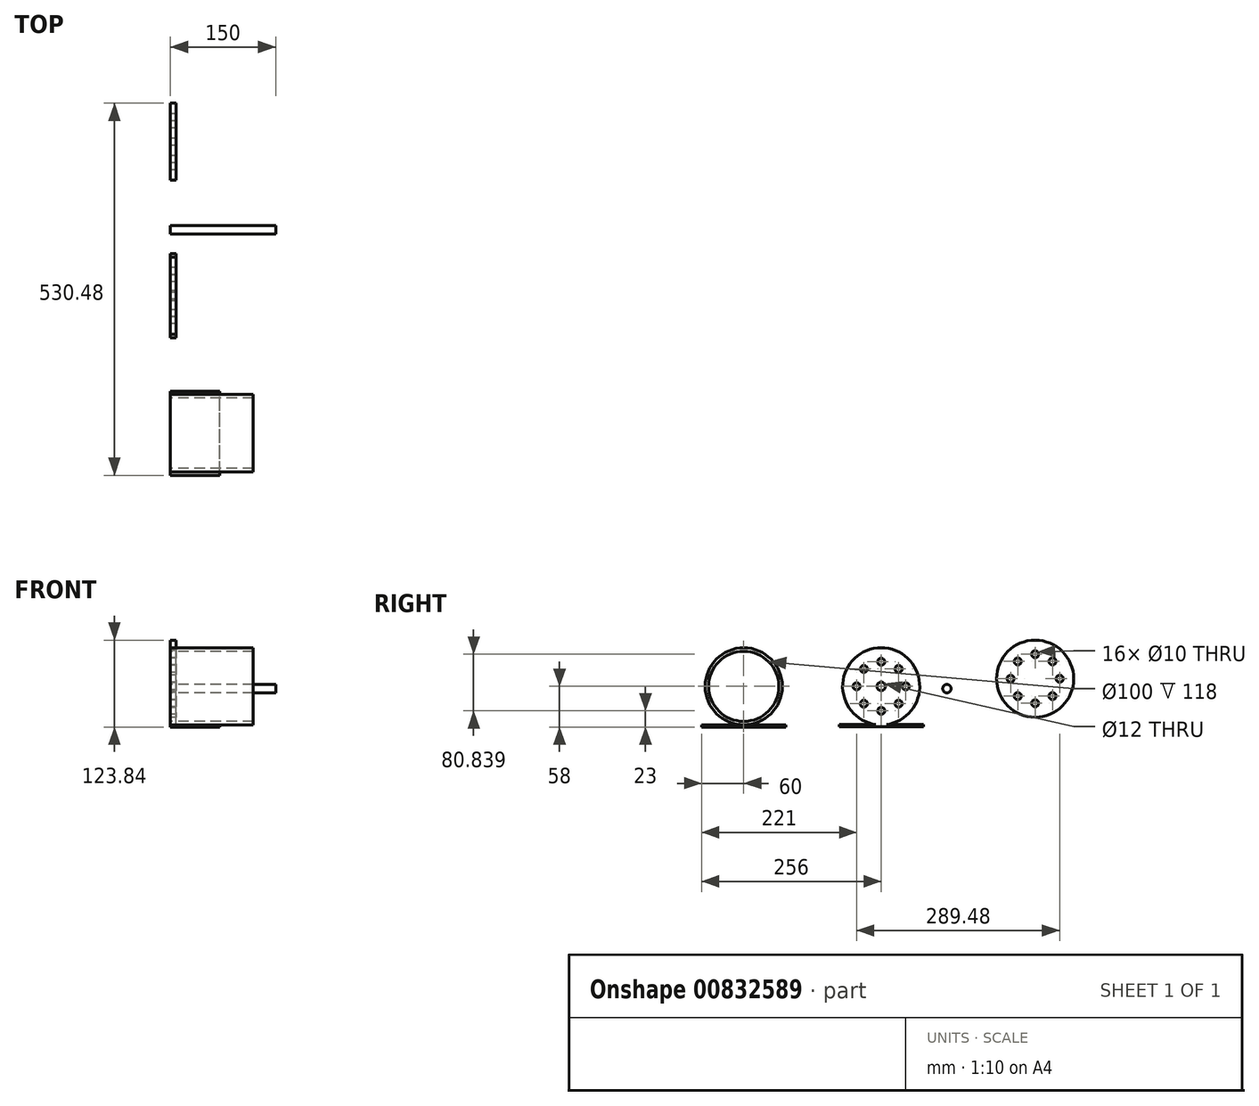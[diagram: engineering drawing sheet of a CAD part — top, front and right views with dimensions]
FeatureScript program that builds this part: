
annotation { "Feature Type Name" : "Feature", "Feature Type Description" : "" }
export const myFeature = defineFeature(function(context is Context, id is Id, definition is map)
    precondition{}
    {
        {
            var Q0;
            Q0=qCreatedBy(makeId("Right.planeOp"),FACE);
            var sketch = newSketch(context, id + "F0", { "sketchPlane" : qUnion([Q0])});
            skArc(sketch, "E0", {"start": v(7.4, -54.5) * mm, "mid": v(0, 55) * mm, "end": v(-7.4, -54.5) * mm});
            skCircle(sketch, "E1", {"center": v(0, 0) * mm, "radius": 6 * mm});
            skCircle(sketch, "E2", {"center": v(0, 35) * mm, "radius": 5 * mm});
            skCircle(sketch, "E3.1.0", {"center": v(-24.75, 24.75) * mm, "radius": 5 * mm});
            skCircle(sketch, "E3.2.0", {"center": v(-35, 0) * mm, "radius": 5 * mm});
            skCircle(sketch, "E3.3.0", {"center": v(-24.75, -24.75) * mm, "radius": 5 * mm});
            skCircle(sketch, "E3.4.0", {"center": v(0, -35) * mm, "radius": 5 * mm});
            skCircle(sketch, "E3.5.0", {"center": v(24.75, -24.75) * mm, "radius": 5 * mm});
            skCircle(sketch, "E3.6.0", {"center": v(35, 0) * mm, "radius": 5 * mm});
            skCircle(sketch, "E3.7.0", {"center": v(24.75, 24.75) * mm, "radius": 5 * mm});
            skLineSegment(sketch, "E4", {"start": v(0, 0) * mm, "end": v(0, -55) * mm});
            skLineSegment(sketch, "E5", {"start": v(60, -55) * mm, "end": v(60, -57.5) * mm});
            skLineSegment(sketch, "E6", {"start": v(60, -57.5) * mm, "end": v(-60, -57.5) * mm});
            skLineSegment(sketch, "E7", {"start": v(-60, -57.5) * mm, "end": v(-60, -54.5) * mm});
            skLineSegment(sketch, "E8", {"start": v(-60, -54.5) * mm, "end": v(-7.4, -54.5) * mm});
            skLineSegment(sketch, "E9", {"start": v(7.4, -54.5) * mm, "end": v(60, -54.5) * mm});
            skLineSegment(sketch, "E10", {"start": v(60, -54.5) * mm, "end": v(60, -55) * mm});
            skPoint(sketch, "E11.orphan", {"position": v(0, -54.5) * mm});
            skSolve(sketch);
        }
        {
            var Q0;
            Q0=makeQuery(id+"F0.imprint","IMPRINT",FACE,{"disambiguationData":[TD([[makeQuery(id+"F0.imprint","IMPRINT",EDGE,{"derivedFrom":sQuery(id+"F0.wireOp",EDGE,"E0")}),1.0]])]});
            extrude(context, id + "F1", {"entities" : qUnion([Q0]), "depth" : 8 * mm, "offsetDistance" : 25 * mm});
        }
        {
            var Q0;
            Q0=qCreatedBy(makeId("Right.planeOp"),FACE);
            var sketch = newSketch(context, id + "F2", { "sketchPlane" : qUnion([Q0])});
            skCircle(sketch, "E12", {"center": v(93.73, -3.28) * mm, "radius": 6 * mm});
            skSolve(sketch);
        }
        {
            var Q0;
            Q0=makeQuery(id+"F2.imprint","IMPRINT",FACE,{"disambiguationData":[TD([[makeQuery(id+"F2.imprint","IMPRINT",EDGE,{"derivedFrom":sQuery(id+"F2.wireOp",EDGE,"E12")}),1.0]])]});
            extrude(context, id + "F3", {"entities" : qUnion([Q0]), "depth" : 150 * mm, "offsetDistance" : 25 * mm});
        }
        {
            var Q0;
            Q0=qCreatedBy(makeId("Right.planeOp"),FACE);
            var sketch = newSketch(context, id + "F4", { "sketchPlane" : qUnion([Q0])});
            skCircle(sketch, "E13", {"center": v(219.48, 10.84) * mm, "radius": 55 * mm});
            skCircle(sketch, "E14", {"center": v(219.48, 45.84) * mm, "radius": 5 * mm});
            skCircle(sketch, "E15.1.0", {"center": v(194.73, 35.59) * mm, "radius": 5 * mm});
            skCircle(sketch, "E15.2.0", {"center": v(184.48, 10.84) * mm, "radius": 5 * mm});
            skCircle(sketch, "E15.3.0", {"center": v(194.73, -13.9) * mm, "radius": 5 * mm});
            skCircle(sketch, "E15.4.0", {"center": v(219.48, -24.16) * mm, "radius": 5 * mm});
            skCircle(sketch, "E15.5.0", {"center": v(244.23, -13.9) * mm, "radius": 5 * mm});
            skCircle(sketch, "E15.6.0", {"center": v(254.48, 10.84) * mm, "radius": 5 * mm});
            skCircle(sketch, "E15.7.0", {"center": v(244.23, 35.59) * mm, "radius": 5 * mm});
            skSolve(sketch);
        }
        {
            var Q0;
            Q0=makeQuery(id+"F4.imprint","IMPRINT",FACE,{"disambiguationData":[TD([[makeQuery(id+"F4.imprint","IMPRINT",EDGE,{"derivedFrom":sQuery(id+"F4.wireOp",EDGE,"E13")}),1.0]])]});
            extrude(context, id + "F5", {"entities" : qUnion([Q0]), "depth" : 8 * mm, "offsetDistance" : 25 * mm});
        }
        {
            var Q0;
            Q0=qCreatedBy(makeId("Right.planeOp"),FACE);
            var sketch = newSketch(context, id + "F6", { "sketchPlane" : qUnion([Q0])});
            skCircle(sketch, "E16", {"center": v(-196, 0) * mm, "radius": 55 * mm});
            skCircle(sketch, "E17", {"center": v(-196, 0) * mm, "radius": 50 * mm});
            skLineSegment(sketch, "E18", {"start": v(-196, -55) * mm, "end": v(-136, -55) * mm});
            skLineSegment(sketch, "E19", {"start": v(-136, -55) * mm, "end": v(-136, -58) * mm});
            skLineSegment(sketch, "E20", {"start": v(-256, -58) * mm, "end": v(-256, -55) * mm});
            skLineSegment(sketch, "E21", {"start": v(-256, -55) * mm, "end": v(-196, -55) * mm});
            skLineSegment(sketch, "E22", {"start": v(-256, -58) * mm, "end": v(-136, -58) * mm});
            skSolve(sketch);
        }
        {
            var Q0;
            Q0=makeQuery(id+"F6.imprint","IMPRINT",FACE,{"disambiguationData":[TD([[makeQuery(id+"F6.imprint","IMPRINT",EDGE,{"derivedFrom":sQuery(id+"F6.wireOp",EDGE,"E17")}),-1.0]])]});
            extrude(context, id + "F7", {"entities" : qUnion([Q0]), "depth" : 118 * mm, "offsetDistance" : 25 * mm});
        }
        {
            var Q0;
            Q0=makeQuery(id+"F6.imprint","IMPRINT",FACE,{"disambiguationData":[TD([[makeQuery(id+"F6.imprint","IMPRINT",EDGE,{"derivedFrom":sQuery(id+"F6.wireOp",EDGE,"E18")}),-1.0]])]});
            extrude(context, id + "F8", {"entities" : qUnion([Q0]), "operationType" : NewBodyOperationType.ADD, "depth" : 70 * mm, "offsetDistance" : 25 * mm});
        }
    });
